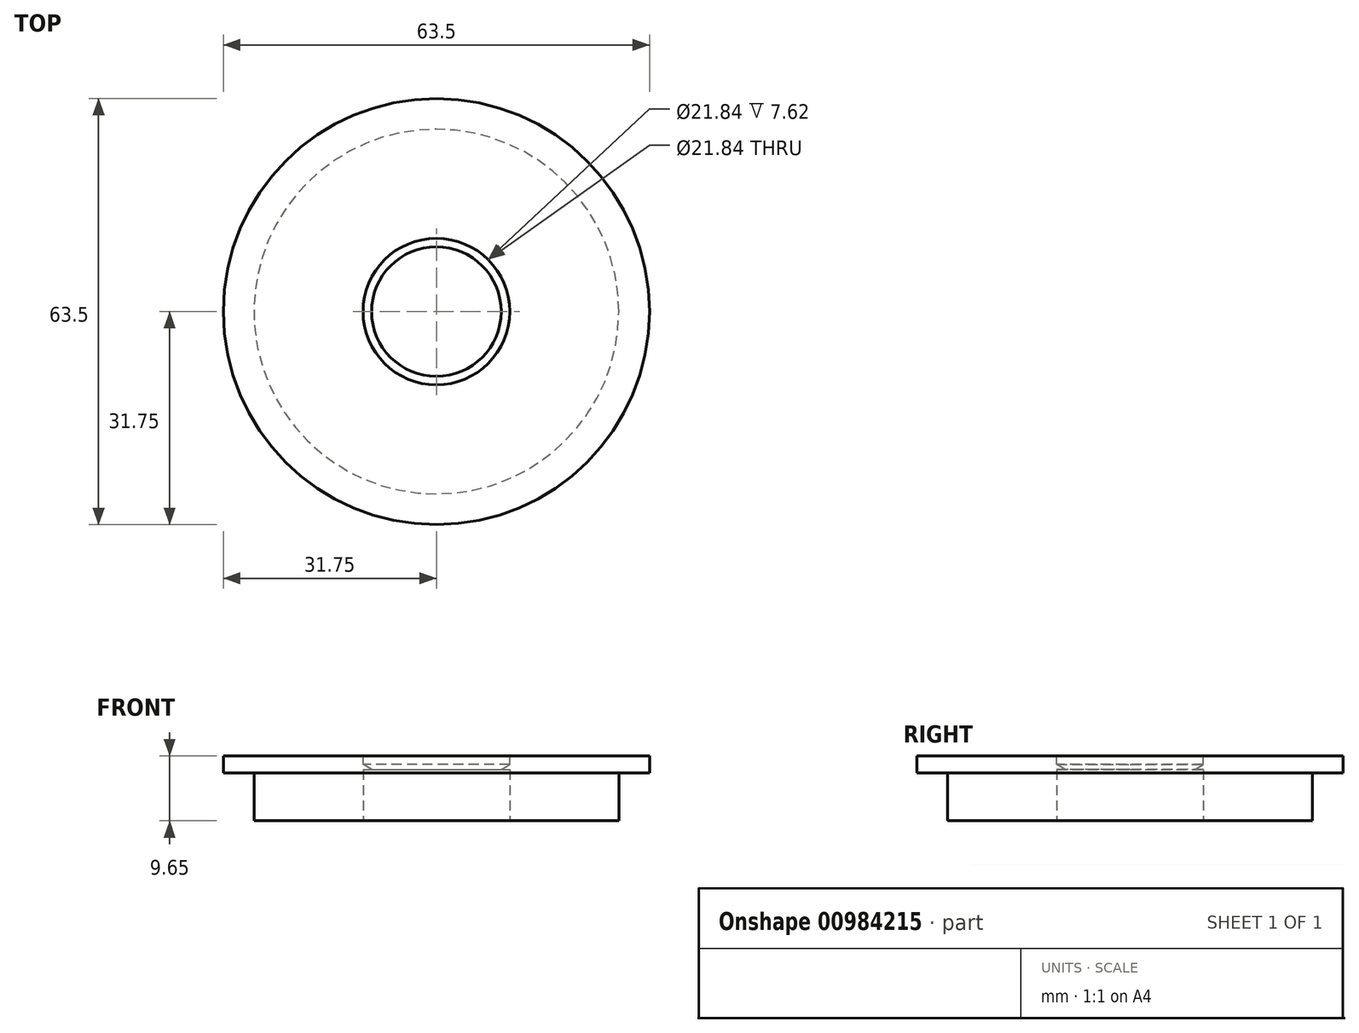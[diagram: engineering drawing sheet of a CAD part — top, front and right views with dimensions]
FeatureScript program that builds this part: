
annotation { "Feature Type Name" : "Feature", "Feature Type Description" : "" }
export const myFeature = defineFeature(function(context is Context, id is Id, definition is map)
    precondition{}
    {
        {
            var Q0;
            Q0=qCreatedBy(makeId("Top.planeOp"),FACE);
            var sketch = newSketch(context, id + "F0", { "sketchPlane" : qUnion([Q0])});
            skCircle(sketch, "E0", {"center": v(0, 0) * mm, "radius": 27.18 * mm});
            skSolve(sketch);
        }
        {
            var Q0;
            Q0=makeQuery(id+"F0.imprint","IMPRINT",FACE,{"disambiguationData":[TD([[makeQuery(id+"F0.imprint","IMPRINT",EDGE,{"derivedFrom":sQuery(id+"F0.wireOp",EDGE,"E0")}),1.0]])]});
            extrude(context, id + "F1", {"entities" : qUnion([Q0]), "depth" : 7.11 * mm, "offsetDistance" : 25.4 * mm});
        }
        {
            var Q0;
            Q0=makeQuery(id+"F1.opExtrude","CAP_FACE",FACE,{"disambiguationData":[OSD([sQuery(id+"F0.wireOp",EDGE,"E0")])],"isStart":false});
            var sketch = newSketch(context, id + "F2", { "sketchPlane" : qUnion([Q0])});
            skCircle(sketch, "E1", {"center": v(0, 0) * mm, "radius": 31.75 * mm});
            skSolve(sketch);
        }
        {
            var Q0;
            Q0 = qSketchRegion(id + "F2", true);
            extrude(context, id + "F3", {"entities" : qUnion([Q0]), "operationType" : NewBodyOperationType.ADD, "depth" : 2.54 * mm, "offsetDistance" : 25.4 * mm});
        }
        {
            var Q0;
            Q0=makeQuery(id+"F1.opExtrude","CAP_FACE",FACE,{"disambiguationData":[OSD([sQuery(id+"F0.wireOp",EDGE,"E0")])],"isStart":true});
            var sketch = newSketch(context, id + "F4", { "sketchPlane" : qUnion([Q0])});
            skPoint(sketch, "E2", {"position": v(0, 0) * mm});
            skSolve(sketch);
        }
        {
            var Q0;
            Q0=sQuery(id+"F4.wireOp",VERTEX,"E2");
            var Q1;
            Q1=makeQuery(id+"F1.opExtrude","SWEPT_BODY",BODY,{"disambiguationData":[OSD([sQuery(id+"F0.wireOp",EDGE,"E0")])]});
            hole(context, id + "F5", {"style" : HoleStyle.C_BORE, "endStyle" : HoleEndStyle.BLIND, "holeDiameter" : 19.3 * mm, "cBoreDiameter" : 21.84 * mm, "cBoreDepth" : 7.62 * mm, "majorDiameter" : 6.35 * mm, "holeDepth" : 7.62 * mm, "isTappedThrough" : true, "tappedDepth" : 12.7 * mm, "tapClearance" : 3, "locations" : qUnion([Q0]), "scope" : qUnion([Q1])});
        }
        {
            var Q0;
            Q0=makeQuery(id+"F3.opExtrude","CAP_FACE",FACE,{"disambiguationData":[OSD([sQuery(id+"F2.wireOp",EDGE,"E1")])],"isStart":false});
            var sketch = newSketch(context, id + "F6", { "sketchPlane" : qUnion([Q0])});
            skPoint(sketch, "E3", {"position": v(0, 0) * mm});
            skSolve(sketch);
        }
        {
            var Q0;
            Q0=sQuery(id+"F6.wireOp",VERTEX,"E3");
            var Q1;
            Q1=makeQuery(id+"F1.opExtrude","SWEPT_BODY",BODY,{"disambiguationData":[OSD([sQuery(id+"F0.wireOp",EDGE,"E0")])]});
            hole(context, id + "F7", {"style" : HoleStyle.SIMPLE, "endStyle" : HoleEndStyle.BLIND, "holeDiameter" : 21.84 * mm, "majorDiameter" : 6.35 * mm, "holeDepth" : 1.27 * mm, "isTappedThrough" : true, "tappedDepth" : 12.7 * mm, "tapClearance" : 3, "locations" : qUnion([Q0]), "scope" : qUnion([Q1])});
        }
    });
